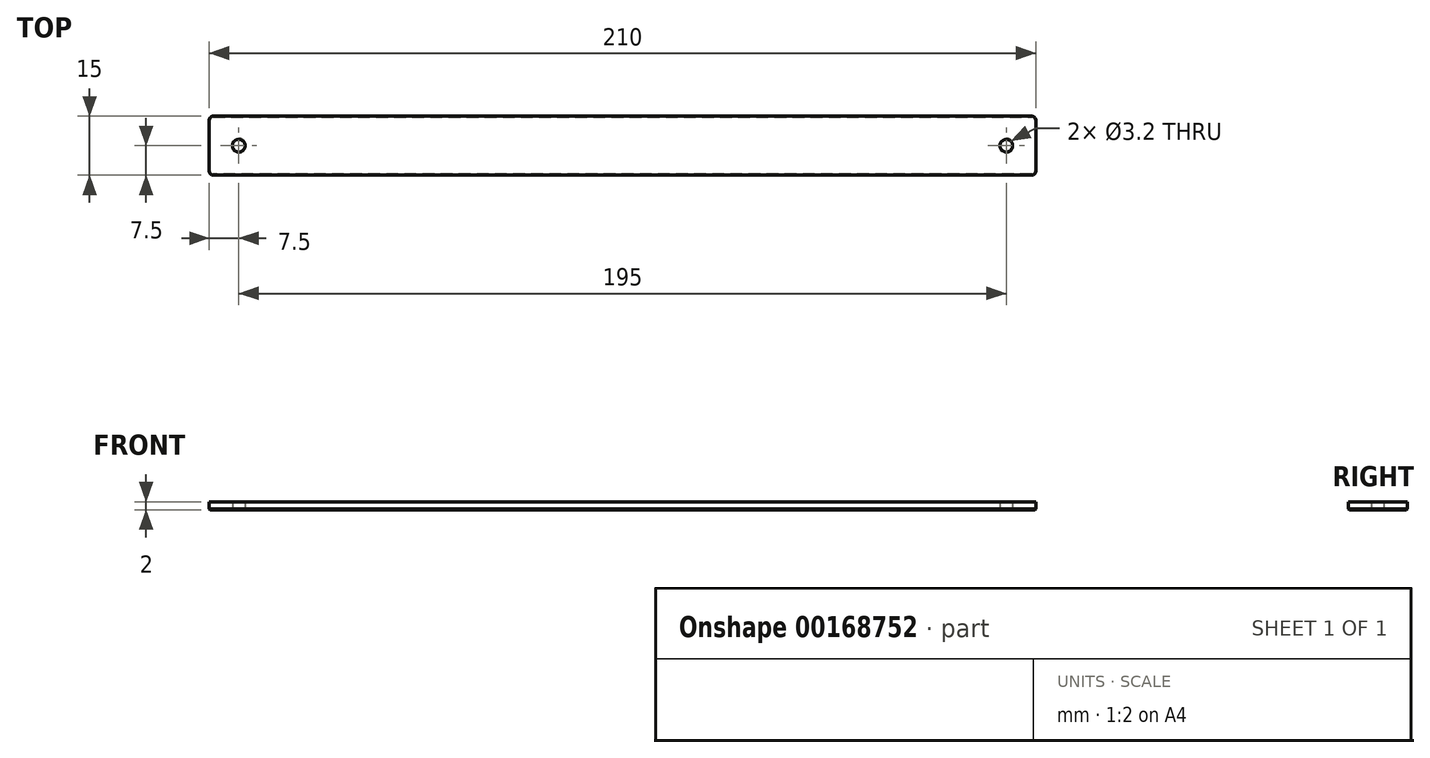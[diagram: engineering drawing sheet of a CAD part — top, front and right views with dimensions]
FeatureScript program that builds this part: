
annotation { "Feature Type Name" : "Feature", "Feature Type Description" : "" }
export const myFeature = defineFeature(function(context is Context, id is Id, definition is map)
    precondition{}
    {
        {
            var Q0;
            Q0=qCreatedBy(makeId("Top.planeOp"),FACE);
            var sketch = newSketch(context, id + "F0", { "sketchPlane" : qUnion([Q0])});
            skLineSegment(sketch, "E0", {"start": v(-97.5, 0) * mm, "end": v(97.5, 0) * mm, "construction": true});
            skLineSegment(sketch, "E1.bottom", {"start": v(105, -7.5) * mm, "end": v(-105, -7.5) * mm});
            skLineSegment(sketch, "E1.top", {"start": v(105, 7.5) * mm, "end": v(-105, 7.5) * mm});
            skLineSegment(sketch, "E1.left", {"start": v(105, -7.5) * mm, "end": v(105, 7.5) * mm});
            skLineSegment(sketch, "E1.right", {"start": v(-105, -7.5) * mm, "end": v(-105, 7.5) * mm});
            skPoint(sketch, "E1.middle", {"position": v(0, 0) * mm});
            skCircle(sketch, "E2", {"center": v(-97.5, 0) * mm, "radius": 1.6 * mm});
            skCircle(sketch, "E3", {"center": v(97.5, 0) * mm, "radius": 1.6 * mm});
            skSolve(sketch);
        }
        {
            var Q0;
            Q0=makeQuery(id+"F0.imprint","IMPRINT",FACE,{"disambiguationData":[TD([[makeQuery(id+"F0.imprint","IMPRINT",EDGE,{"derivedFrom":sQuery(id+"F0.wireOp",EDGE,"E1.bottom")}),-1.0]])]});
            extrude(context, id + "F1", {"entities" : qUnion([Q0]), "depth" : 2 * mm});
        }
        {
            var Q0;
            Q0=makeQuery(id+"F1.opExtrude","SWEPT_EDGE",EDGE,{"disambiguationData":[OSD([sQuery(id+"F0.wireOp",EDGE,"E1.top"),sQuery(id+"F0.wireOp",EDGE,"E1.right")])]});
            var Q1;
            Q1=makeQuery(id+"F1.opExtrude","SWEPT_EDGE",EDGE,{"disambiguationData":[OSD([sQuery(id+"F0.wireOp",EDGE,"E1.bottom"),sQuery(id+"F0.wireOp",EDGE,"E1.right")])]});
            var Q2;
            Q2=makeQuery(id+"F1.opExtrude","SWEPT_EDGE",EDGE,{"disambiguationData":[OSD([sQuery(id+"F0.wireOp",EDGE,"E1.top"),sQuery(id+"F0.wireOp",EDGE,"E1.left")])]});
            var Q3;
            Q3=makeQuery(id+"F1.opExtrude","SWEPT_EDGE",EDGE,{"disambiguationData":[OSD([sQuery(id+"F0.wireOp",EDGE,"E1.bottom"),sQuery(id+"F0.wireOp",EDGE,"E1.left")])]});
            fillet(context, id + "F2", {"entities" : qUnion([Q0, Q1, Q2, Q3]), "radius" : 1 * mm, "allowEdgeOverflow" : false});
        }
        {
            var Q0;
            Q0=makeQuery(id+"F1.opExtrude","CAP_FACE",FACE,{"disambiguationData":[OSD([sQuery(id+"F0.wireOp",EDGE,"E1.bottom"),sQuery(id+"F0.wireOp",EDGE,"E1.top"),sQuery(id+"F0.wireOp",EDGE,"E1.left"),sQuery(id+"F0.wireOp",EDGE,"E1.right"),sQuery(id+"F0.wireOp",EDGE,"E2"),sQuery(id+"F0.wireOp",EDGE,"E3")])],"isStart":true});
            chamfer(context, id + "F3", {"entities" : qUnion([Q0]), "width" : .25 * mm});
        }
    });
